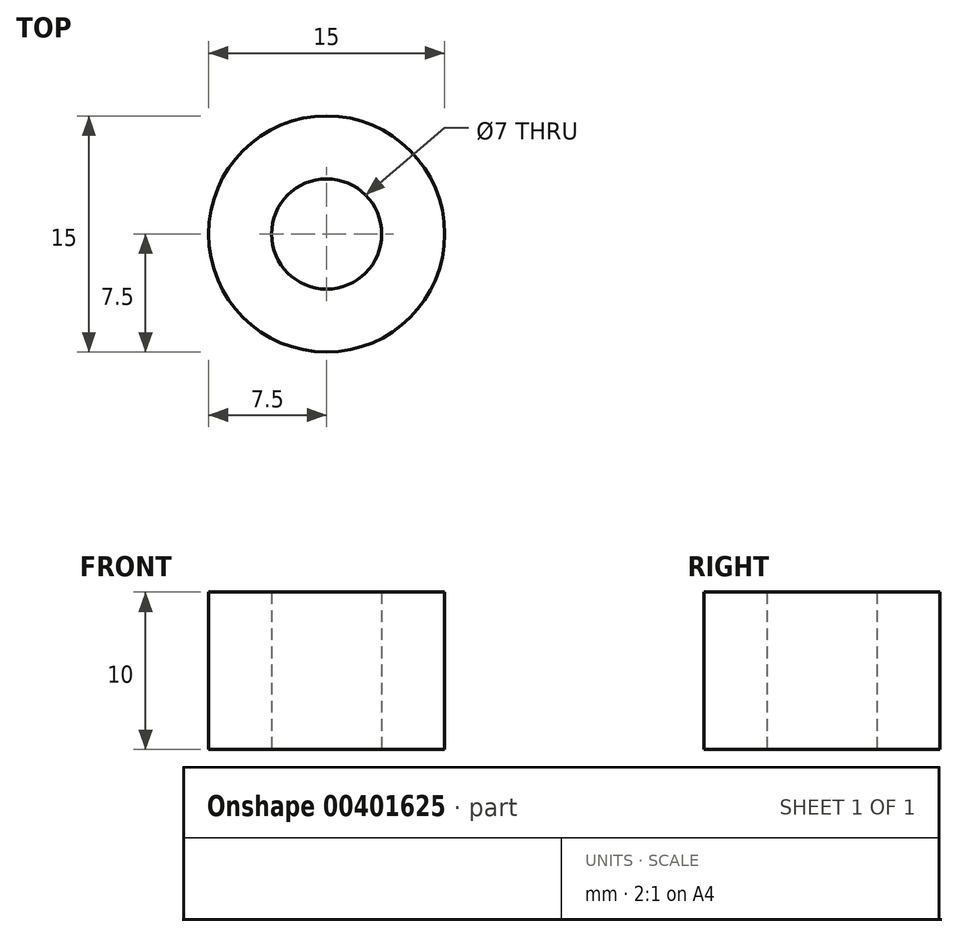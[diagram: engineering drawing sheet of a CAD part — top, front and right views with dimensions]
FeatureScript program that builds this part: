
annotation { "Feature Type Name" : "Feature", "Feature Type Description" : "" }
export const myFeature = defineFeature(function(context is Context, id is Id, definition is map)
    precondition{}
    {
        {
            var Q0;
            Q0=qCreatedBy(makeId("Top.planeOp"),FACE);
            var sketch = newSketch(context, id + "F0", { "sketchPlane" : qUnion([Q0])});
            skCircle(sketch, "E0", {"center": v(0, 0) * mm, "radius": 7.5 * mm});
            skCircle(sketch, "E1", {"center": v(0, 0) * mm, "radius": 3.5 * mm});
            skSolve(sketch);
        }
        {
            var Q0;
            Q0=makeQuery(id+"F0.imprint","IMPRINT",FACE,{"disambiguationData":[TD([[makeQuery(id+"F0.imprint","IMPRINT",EDGE,{"derivedFrom":sQuery(id+"F0.wireOp",EDGE,"E0")}),1.0]])]});
            extrude(context, id + "F1", {"entities" : qUnion([Q0]), "depth" : 10 * mm});
        }
    });
